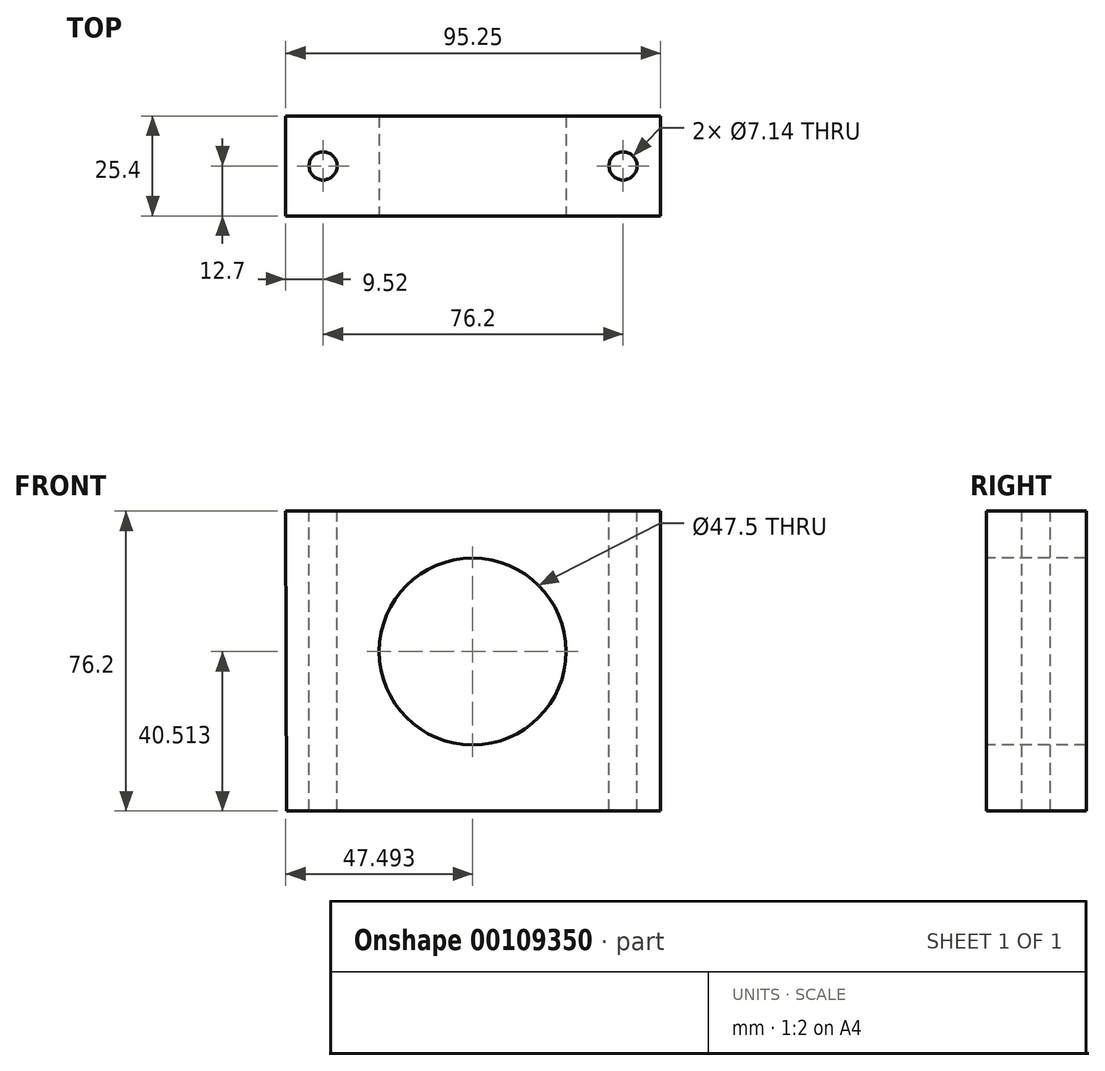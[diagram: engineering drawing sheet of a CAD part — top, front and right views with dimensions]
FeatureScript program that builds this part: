
annotation { "Feature Type Name" : "Feature", "Feature Type Description" : "" }
export const myFeature = defineFeature(function(context is Context, id is Id, definition is map)
    precondition{}
    {
        {
            var Q0;
            Q0=qCreatedBy(makeId("Front.planeOp"),FACE);
            var sketch = newSketch(context, id + "F0", { "sketchPlane" : qUnion([Q0])});
            skLineSegment(sketch, "E0", {"start": v(-38.04, 37.99) * mm, "end": v(57.2, 37.99) * mm});
            skLineSegment(sketch, "E1", {"start": v(57.2, 37.99) * mm, "end": v(57.2, -38.21) * mm});
            skLineSegment(sketch, "E2", {"start": v(57.2, -38.21) * mm, "end": v(-37.82, -38.21) * mm});
            skLineSegment(sketch, "E3", {"start": v(-37.82, -38.21) * mm, "end": v(-38.04, 37.99) * mm});
            skSolve(sketch);
        }
        {
            var Q0;
            Q0 = qSketchRegion(id + "F0", true);
            extrude(context, id + "F1", {"entities" : qUnion([Q0]), "depth" : 25.4 * mm});
        }
        {
            var Q0;
            Q0=makeQuery(id+"F1.opExtrude","CAP_FACE",FACE,{"disambiguationData":[OSD([sQuery(id+"F0.wireOp",EDGE,"E0"),sQuery(id+"F0.wireOp",EDGE,"E1"),sQuery(id+"F0.wireOp",EDGE,"E2"),sQuery(id+"F0.wireOp",EDGE,"E3")])],"isStart":false});
            var sketch = newSketch(context, id + "F2", { "sketchPlane" : qUnion([Q0])});
            skCircle(sketch, "E4", {"center": v(9.45, 2.3) * mm, "radius": 23.75 * mm});
            skSolve(sketch);
        }
        {
            var Q0;
            Q0=makeQuery(id+"F2.imprint","IMPRINT",FACE,{"disambiguationData":[TD([[makeQuery(id+"F2.imprint","IMPRINT",EDGE,{"derivedFrom":sQuery(id+"F2.wireOp",EDGE,"E4")}),1.0]])]});
            extrude(context, id + "F3", {"entities" : qUnion([Q0]), "operationType" : NewBodyOperationType.REMOVE, "endBound" : BoundingType.THROUGH_ALL, "oppositeDirection" : true, "depth" : 25.4 * mm});
        }
        {
            var Q0;
            Q0=makeQuery(id+"F1.opExtrude","SWEPT_FACE",FACE,{"disambiguationData":[OSD([sQuery(id+"F0.wireOp",EDGE,"E0")])]});
            var sketch = newSketch(context, id + "F4", { "sketchPlane" : qUnion([Q0])});
            skLineSegment(sketch, "E5", {"start": v(-38.04, -12.7) * mm, "end": v(-28.52, -12.7) * mm, "construction": true});
            skLineSegment(sketch, "E6", {"start": v(57.2, -12.7) * mm, "end": v(47.68, -12.7) * mm, "construction": true});
            skLineSegment(sketch, "E7", {"start": v(47.68, -12.7) * mm, "end": v(57.2, -12.7) * mm, "construction": true});
            skCircle(sketch, "E8", {"center": v(-28.52, -12.7) * mm, "radius": 3.57 * mm});
            skCircle(sketch, "E9", {"center": v(47.68, -12.7) * mm, "radius": 3.57 * mm});
            skSolve(sketch);
        }
        {
            var Q0;
            Q0=makeQuery(id+"F4.imprint","IMPRINT",FACE,{"disambiguationData":[TD([[makeQuery(id+"F4.imprint","IMPRINT",EDGE,{"derivedFrom":sQuery(id+"F4.wireOp",EDGE,"E8")}),1.0]])]});
            var Q1;
            Q1=makeQuery(id+"F4.imprint","IMPRINT",FACE,{"disambiguationData":[TD([[makeQuery(id+"F4.imprint","IMPRINT",EDGE,{"derivedFrom":sQuery(id+"F4.wireOp",EDGE,"E9")}),1.0]])]});
            extrude(context, id + "F5", {"entities" : qUnion([Q0, Q1]), "operationType" : NewBodyOperationType.REMOVE, "endBound" : BoundingType.THROUGH_ALL, "oppositeDirection" : true, "depth" : 25.4 * mm});
        }
    });
